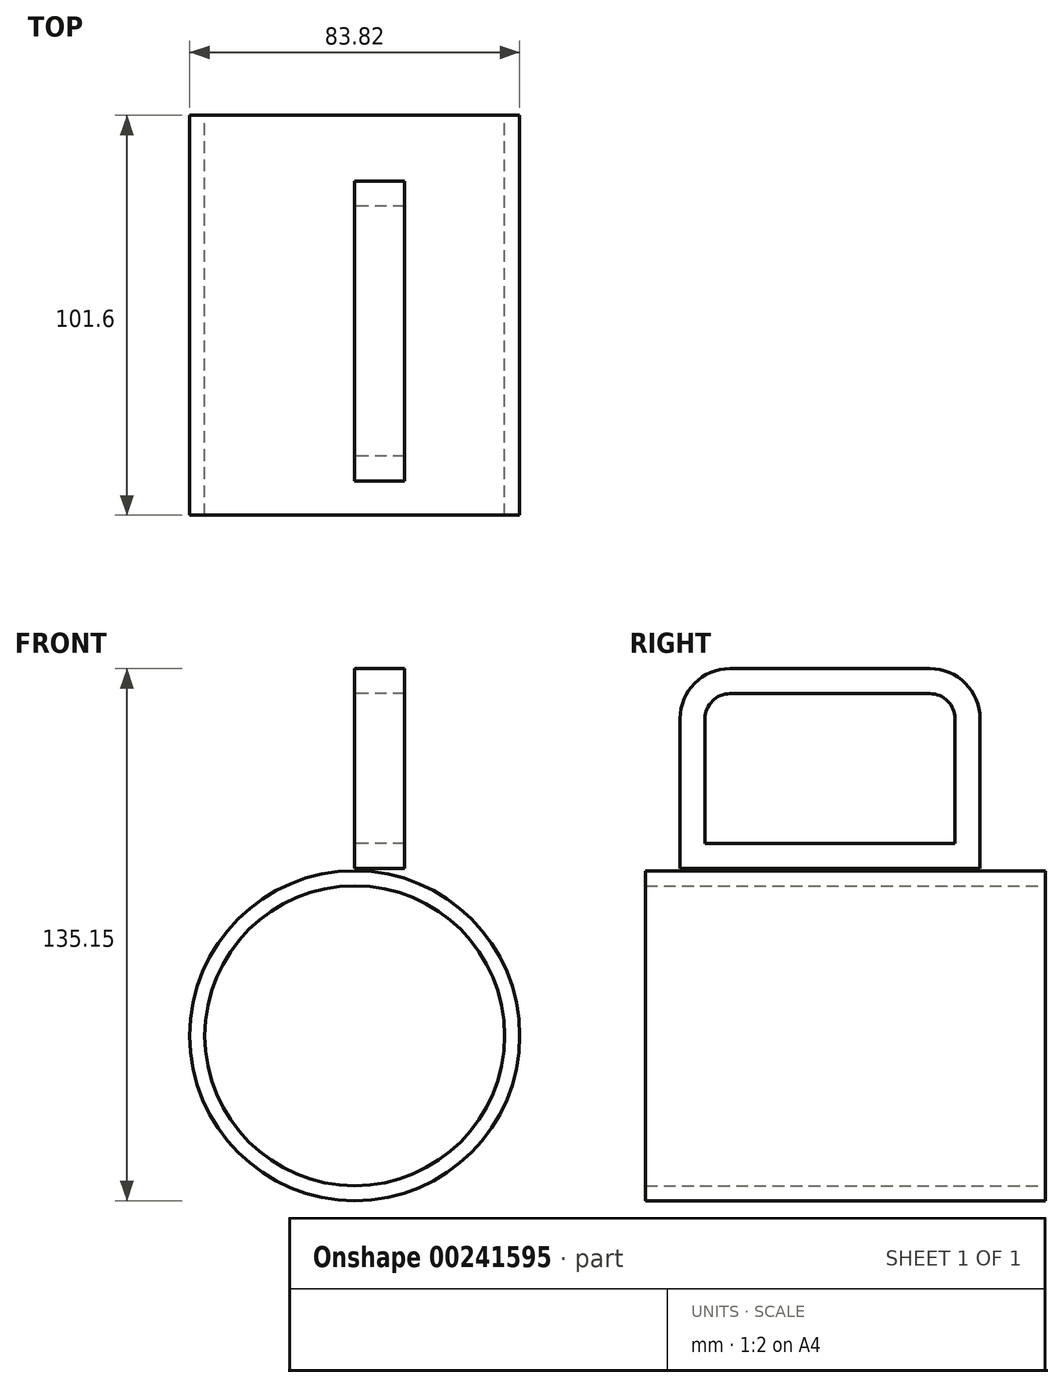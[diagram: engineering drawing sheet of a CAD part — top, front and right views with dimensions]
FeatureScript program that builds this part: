
annotation { "Feature Type Name" : "Feature", "Feature Type Description" : "" }
export const myFeature = defineFeature(function(context is Context, id is Id, definition is map)
    precondition{}
    {
        {
            var Q0;
            Q0=qCreatedBy(makeId("Front.planeOp"),FACE);
            var sketch = newSketch(context, id + "F0", { "sketchPlane" : qUnion([Q0])});
            skCircle(sketch, "E0", {"center": v(0, 0) * mm, "radius": 38.1 * mm});
            skCircle(sketch, "E1.0", {"center": v(0, 0) * mm, "radius": 41.91 * mm});
            skSolve(sketch);
        }
        {
            var Q0;
            Q0=makeQuery(id+"F0.imprint","IMPRINT",FACE,{"disambiguationData":[TD([[makeQuery(id+"F0.imprint","IMPRINT",EDGE,{"derivedFrom":sQuery(id+"F0.wireOp",EDGE,"E0")}),-1.0]])]});
            extrude(context, id + "F1", {"entities" : qUnion([Q0]), "depth" : 101.6 * mm});
        }
        {
            var Q0;
            Q0=qCreatedBy(makeId("Right.planeOp"),FACE);
            var sketch = newSketch(context, id + "F2", { "sketchPlane" : qUnion([Q0])});
            skLineSegment(sketch, "E2.bottom", {"start": v(-92.88, 42.44) * mm, "end": v(-16.68, 42.44) * mm});
            skLineSegment(sketch, "E2.top", {"start": v(-80.18, 93.24) * mm, "end": v(-29.38, 93.24) * mm});
            skLineSegment(sketch, "E2.left", {"start": v(-92.88, 42.44) * mm, "end": v(-92.88, 80.54) * mm});
            skLineSegment(sketch, "E2.right", {"start": v(-16.68, 42.44) * mm, "end": v(-16.68, 80.54) * mm});
            skPoint(sketch, "E3.visualSharp", {"position": v(-92.88, 93.24) * mm});
            skArc(sketch, "E3.filletArc", {"start": v(-80.18, 93.24) * mm, "mid": v(-89.16, 89.52) * mm, "end": v(-92.88, 80.54) * mm});
            skPoint(sketch, "E4.visualSharp", {"position": v(-16.68, 93.24) * mm});
            skArc(sketch, "E4.filletArc", {"start": v(-16.68, 80.54) * mm, "mid": v(-20.4, 89.52) * mm, "end": v(-29.38, 93.24) * mm});
            skArc(sketch, "E5.0", {"start": v(-80.18, 86.9) * mm, "mid": v(-84.67, 85.03) * mm, "end": v(-86.53, 80.54) * mm});
            skArc(sketch, "E5.1", {"start": v(-23.03, 80.54) * mm, "mid": v(-24.89, 85.03) * mm, "end": v(-29.38, 86.9) * mm});
            skLineSegment(sketch, "E5.2", {"start": v(-23.03, 48.8) * mm, "end": v(-23.03, 80.54) * mm});
            skLineSegment(sketch, "E5.3", {"start": v(-80.18, 86.9) * mm, "end": v(-29.38, 86.9) * mm});
            skLineSegment(sketch, "E5.4", {"start": v(-86.53, 48.8) * mm, "end": v(-23.03, 48.8) * mm});
            skLineSegment(sketch, "E5.5", {"start": v(-86.53, 48.8) * mm, "end": v(-86.53, 80.54) * mm});
            skSolve(sketch);
        }
        {
            var Q0;
            Q0=makeQuery(id+"F2.imprint","IMPRINT",FACE,{"disambiguationData":[TD([[makeQuery(id+"F2.imprint","IMPRINT",EDGE,{"derivedFrom":sQuery(id+"F2.wireOp",EDGE,"E2.bottom")}),1.0]])]});
            extrude(context, id + "F3", {"entities" : qUnion([Q0]), "depth" : 12.7 * mm});
        }
    });
